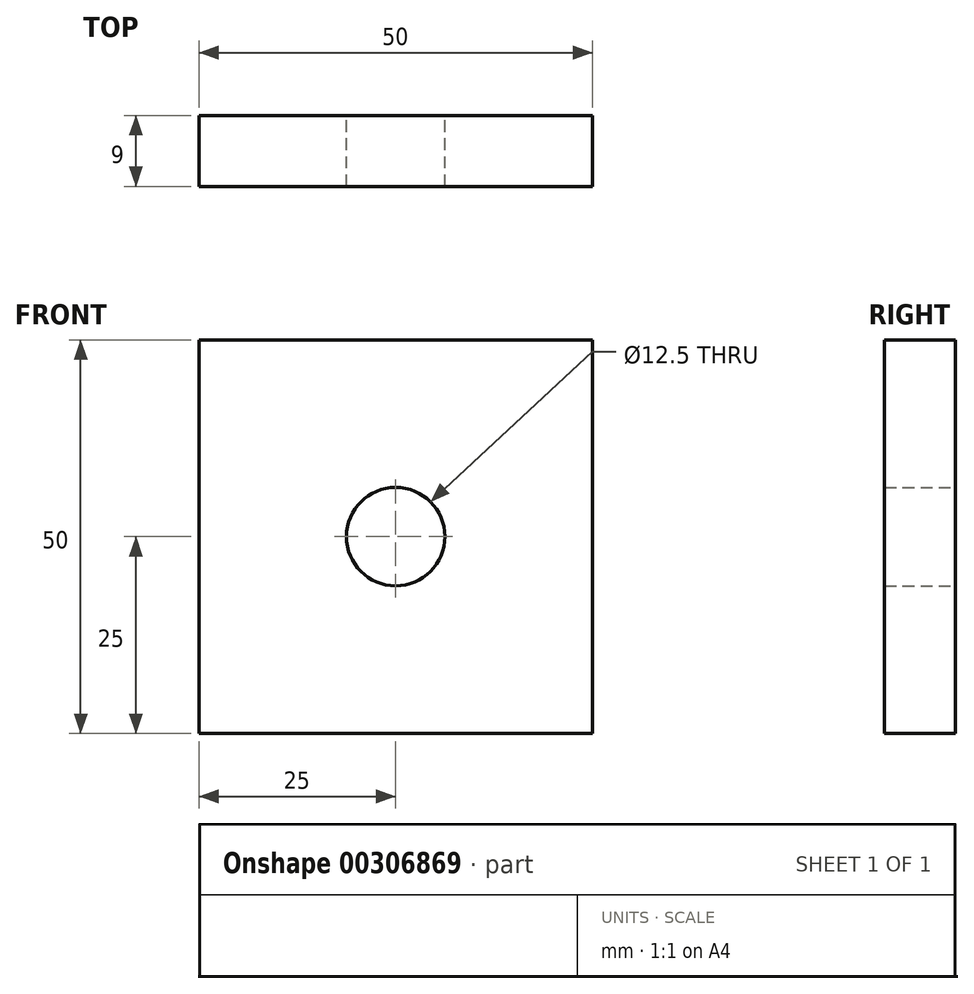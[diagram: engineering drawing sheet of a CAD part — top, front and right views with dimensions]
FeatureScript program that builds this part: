
annotation { "Feature Type Name" : "Feature", "Feature Type Description" : "" }
export const myFeature = defineFeature(function(context is Context, id is Id, definition is map)
    precondition{}
    {
        {
            var Q0;
            Q0=qCreatedBy(makeId("Front.planeOp"),FACE);
            var sketch = newSketch(context, id + "F0", { "sketchPlane" : qUnion([Q0])});
            skLineSegment(sketch, "E0.bottom", {"start": v(0, 0) * mm, "end": v(50, 0) * mm});
            skLineSegment(sketch, "E0.top", {"start": v(0, 50) * mm, "end": v(50, 50) * mm});
            skLineSegment(sketch, "E0.left", {"start": v(0, 0) * mm, "end": v(0, 50) * mm});
            skLineSegment(sketch, "E0.right", {"start": v(50, 0) * mm, "end": v(50, 50) * mm});
            skCircle(sketch, "E1", {"center": v(25, 25) * mm, "radius": 6.25 * mm});
            skSolve(sketch);
        }
        {
            var Q0;
            Q0=makeQuery(id+"F0.imprint","IMPRINT",FACE,{"disambiguationData":[TD([[makeQuery(id+"F0.imprint","IMPRINT",EDGE,{"derivedFrom":sQuery(id+"F0.wireOp",EDGE,"E0.bottom")}),1.0]])]});
            extrude(context, id + "F1", {"entities" : qUnion([Q0]), "depth" : 9 * mm});
        }
    });
